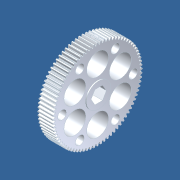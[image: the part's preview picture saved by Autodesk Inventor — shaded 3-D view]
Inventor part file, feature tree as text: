
AUTODESK INVENTOR PART (.ipt)
format: ipt  version: unknown  size: 1,947,648 bytes
history: native  units: in
note: dims shown in document units (in); Inventor stores cm internally (conversion verified against a paired STEP export)
features: extrude x2, sketch x2, other x1, imported_body x1
ambient origin geometry x8: Origin, YZ Plane, XZ Plane, XY Plane, X Axis, Y Axis, Z Axis, Center Point
feature tree (6):
  other  "hex"
  imported_body  "Base1"
  extrude  "Extrusion1"  Depth=0.5625in
  extrude  "Extrusion2"  Depth=1.0in TaperAngle=0.0deg
  sketch  "Sketch1"  dims[d0=0.625in d1=0.5625in]
  sketch  "Sketch2"  dims[d2=2.3622in d4=360.0deg d6=1.0in d7=0.0in d8=0.25in d9=0.525in d10=0.525in d11=2.3622in d13=360.0deg d15=1.0in d16=0.0in]
